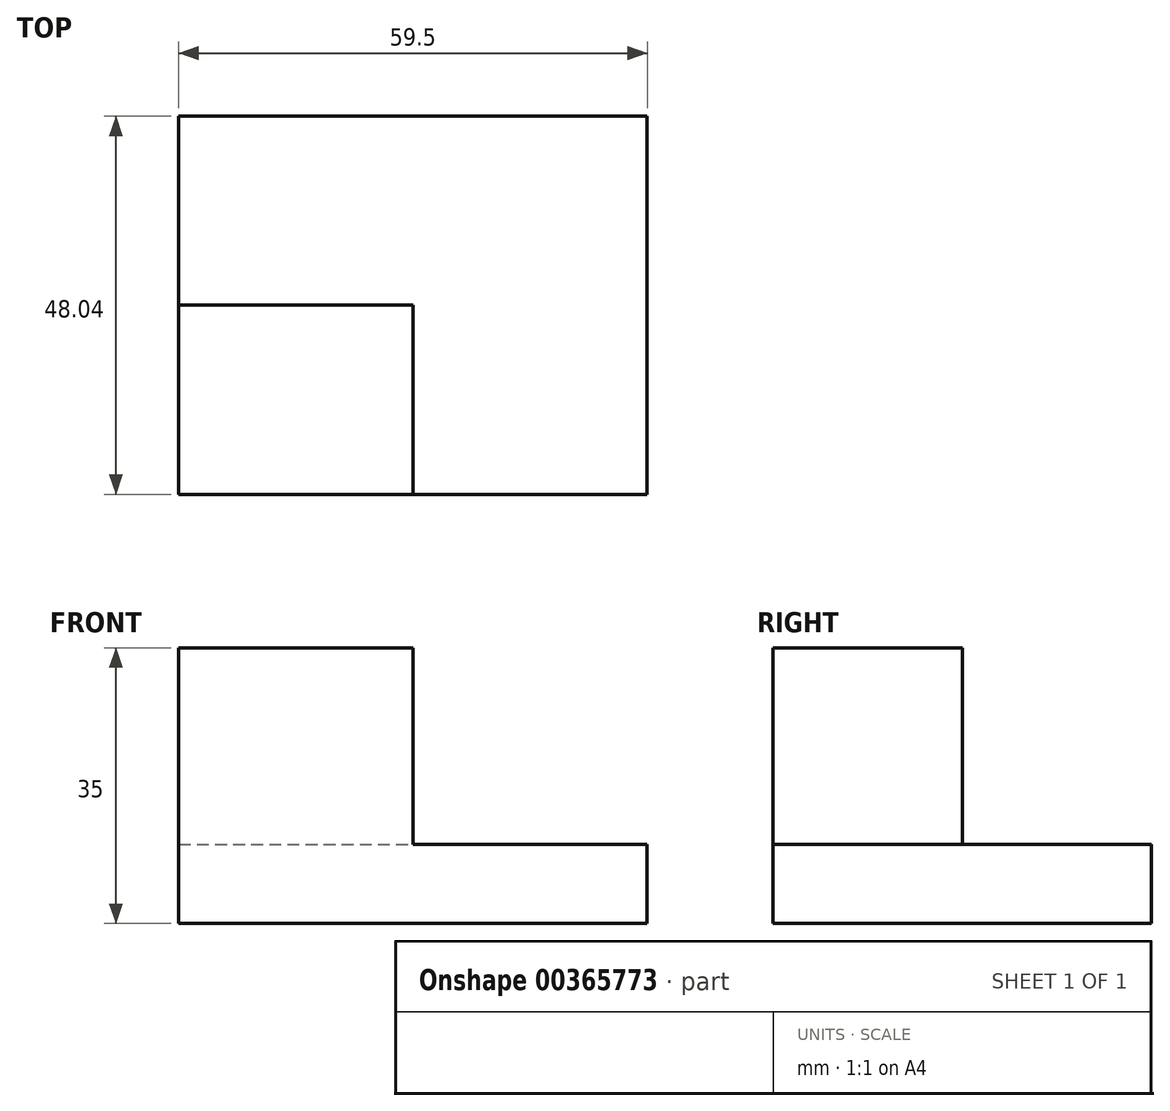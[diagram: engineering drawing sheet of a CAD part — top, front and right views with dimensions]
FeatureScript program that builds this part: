
annotation { "Feature Type Name" : "Feature", "Feature Type Description" : "" }
export const myFeature = defineFeature(function(context is Context, id is Id, definition is map)
    precondition{}
    {
        {
            var Q0;
            Q0=qCreatedBy(makeId("Top.planeOp"),FACE);
            var sketch = newSketch(context, id + "F0", { "sketchPlane" : qUnion([Q0])});
            skLineSegment(sketch, "E0.bottom", {"start": v(0, 0) * mm, "end": v(59.5, 0) * mm});
            skLineSegment(sketch, "E0.top", {"start": v(0, 48.04) * mm, "end": v(59.5, 48.04) * mm});
            skLineSegment(sketch, "E0.left", {"start": v(0, 0) * mm, "end": v(0, 48.04) * mm});
            skLineSegment(sketch, "E0.right", {"start": v(59.5, 0) * mm, "end": v(59.5, 48.04) * mm});
            skSolve(sketch);
        }
        {
            var Q0;
            Q0 = qSketchRegion(id + "F0", true);
            extrude(context, id + "F1", {"entities" : qUnion([Q0]), "depth" : 10 * mm});
        }
        {
            var Q0;
            Q0=makeQuery(id+"F1.opExtrude","CAP_FACE",FACE,{"disambiguationData":[OSD([sQuery(id+"F0.wireOp",EDGE,"E0.bottom"),sQuery(id+"F0.wireOp",EDGE,"E0.top"),sQuery(id+"F0.wireOp",EDGE,"E0.left"),sQuery(id+"F0.wireOp",EDGE,"E0.right")])],"isStart":false});
            var sketch = newSketch(context, id + "F2", { "sketchPlane" : qUnion([Q0])});
            skPoint(sketch, "E1.oppositeSnap0", {"position": v(29.75, 48.04) * mm});
            skPoint(sketch, "E1.oppositeSnap1", {"position": v(59.5, 24.02) * mm});
            skLineSegment(sketch, "E1.bottom", {"start": v(0, 0) * mm, "end": v(29.75, 0) * mm});
            skLineSegment(sketch, "E1.top", {"start": v(0, 24.02) * mm, "end": v(29.75, 24.02) * mm});
            skLineSegment(sketch, "E1.left", {"start": v(0, 0) * mm, "end": v(0, 24.02) * mm});
            skLineSegment(sketch, "E1.right", {"start": v(29.75, 0) * mm, "end": v(29.75, 24.02) * mm});
            skSolve(sketch);
        }
        {
            var Q0;
            Q0 = qSketchRegion(id + "F2", true);
            extrude(context, id + "F3", {"entities" : qUnion([Q0]), "operationType" : NewBodyOperationType.ADD, "depth" : 25 * mm});
        }
    });
